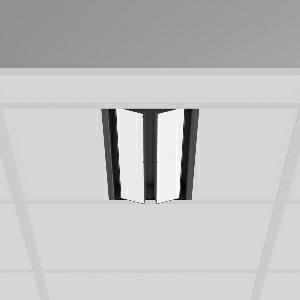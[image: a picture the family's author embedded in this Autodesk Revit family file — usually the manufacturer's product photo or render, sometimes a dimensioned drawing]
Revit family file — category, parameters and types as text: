
# Revit family: tx-move_901735_003_1_76_9fa9
name_source: partatom
category: Lighting Fixtures
units: mm (PartAtom-declared; Revit-internal decimal feet)

## family parameters
Cut with Voids When Loaded = No
Host = Face
Light Source = No
Part Type = Normal
Room Calculation Point = No
Round Connector Dimension = Use Diameter
Shared = No

## types (1)
- MultiLumen 1 (1 x LED Modul 840, 2450 lm, 4000)
    Apparent Load = 35 VA
    Approval mark = CE
    CIE Flux Codes = 47 79 96 100 100
    Color Rendering = 80
    Color Temperature = 4000
    Default Elevation = 1800 mm
    Description = Series: TX-MOVE
Einlege/Einbau-Flächenstrahler. Housing: sheet steel, powder-coated. 2xSwivel range: 90°. High-efficiency LED units with flush-mounted opal diffuser made of non-yellowing PMMA. Symmetrical wide beam light emission. Suitable for laying in grid ceiling module 600. Connected converter included in separate gearbox.Suitable for through-wiring.MultiLumen: Luminous flux adjustable in 3 steps. Accessories: Mounting frame for installation in suspended ceilings. Environmentally friendly and resource-saving due to replaceable and recyclable components. 
Colour: deep black, matt (RAL 9005)
Length: 597 mm
Width: 190 mm
Height: 39 mm
Cut-out length: 577.5 mm
Cut-out width: 174 mm
Recess height: 100 mm
Lamp: LED
Socket: without socket
Colour temperature: 4000K
Colour rendering index (CRI): 80
System power: 35 W
Rated luminous flux: 4900 lm
Luminous efficiency: 140 lm/W
System power 2: 47 W
Rated luminous flux 2: 6450 lm
Luminous efficiency 2: 137 lm/W
System power 3: 68 W
Rated luminous flux 3: 8750 lm
Luminous efficiency 3: 129 lm/W
Control gear: Dimmable EVG, DALI
Protection class: I
Type of protection: IP 20
    Height = 0 mm  [stored 0 ft]
    Lamp = 1 x LED Modul 840
    Lamp Light Flux = 2450 lm
    Lamp count = 1
    Length = 597 mm
    Lifetime = 50000 h
    Luminous efficacy = 140 lm/W
    Manufacturer = RZB
    ModVariant = No
    Model = 901735.003.1.76
    Mounting Place = Ceiling, Wall
    Mounting Type = Recessed
    Number of Poles = 1
    OnlyDefault = Yes
    Power Factor = 1
    Product Name = TX-MOVE
    Product group = Recessed projectors
    ProductGroupID = 401
    Protection Class = Protection class I
    Protection Degree = IP 20
    RLX_Detail_Level = 1
    RLX_Emergency_Light_Flux = 0 lm
    RLX_Emergency_Type = 0
    RLX_Emergency_Type_DB = No
    RlxData = <blob elided: 32701 chars, md5=e2280732>
    Socket = socket
    Standby Power = 0 W
    System Light Flux = 4900 lm
    System Power = 35 W
    Type Comments = MultiLumen 1
    Type Image = 901735.003.jpg
    URL = http://relux.com
    VarID = multilumen_1
    Voltage = 230 V
    Voltage Range = 220-240 V
    Weight = 0.00 kg
    Width = 190 mm  [stored 0.62336 ft]

note: [stored X ft] marks values corroborated as IEEE doubles in the binary element streams (Revit-internal decimal feet)

## geometry (parser evidence)
native form markers: Blend x4, Sweep x17
no freeform markers — native parametric forms only
